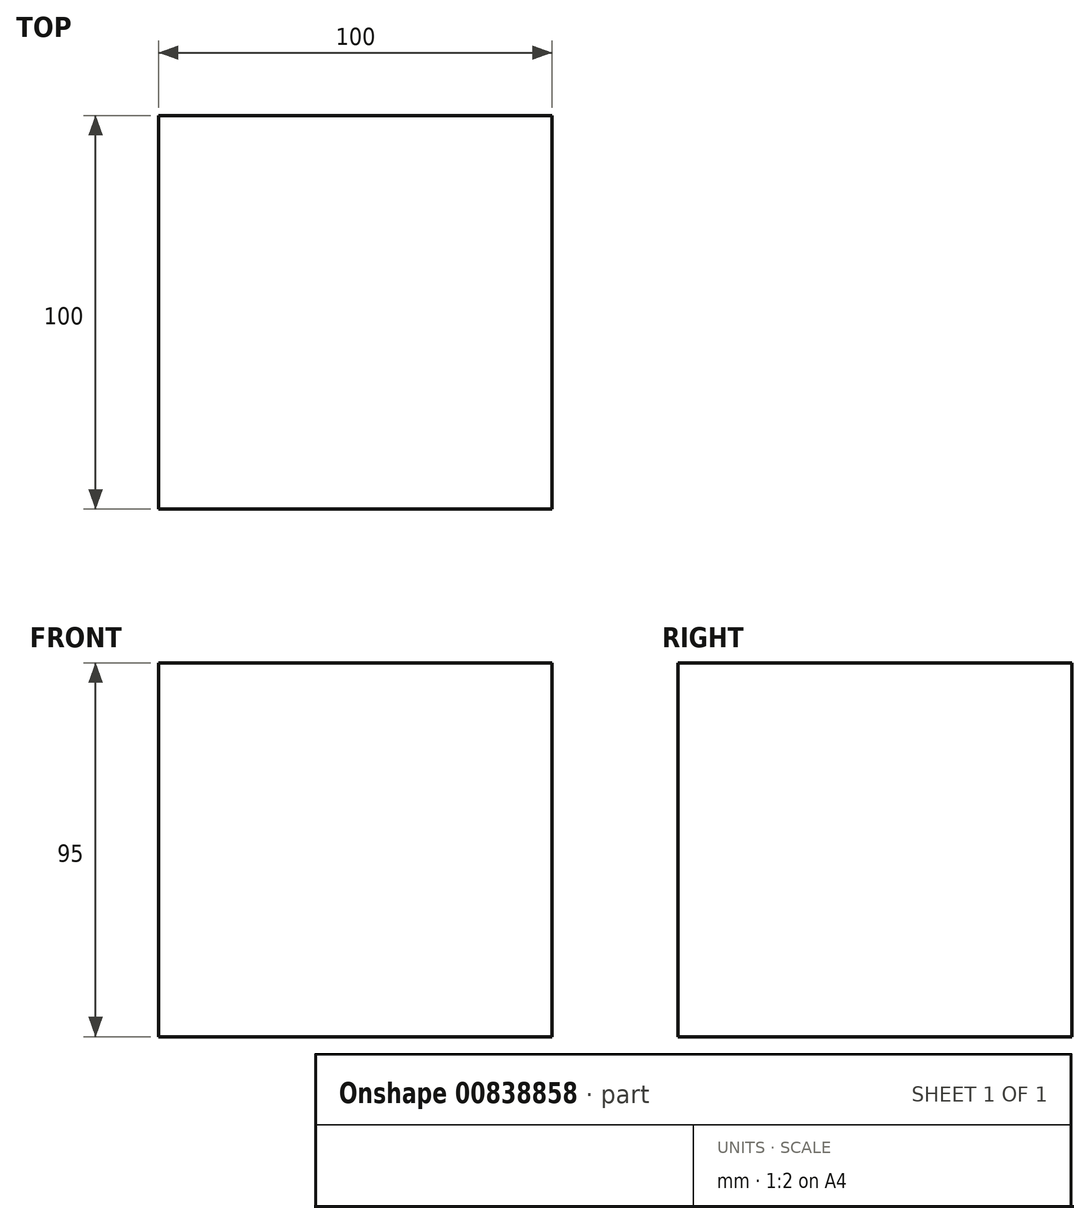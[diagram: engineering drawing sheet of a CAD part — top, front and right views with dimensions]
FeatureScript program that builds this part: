
annotation { "Feature Type Name" : "Feature", "Feature Type Description" : "" }
export const myFeature = defineFeature(function(context is Context, id is Id, definition is map)
    precondition{}
    {
        {
            var Q0;
            Q0=qCreatedBy(makeId("Top.planeOp"),FACE);
            var sketch = newSketch(context, id + "F0", { "sketchPlane" : qUnion([Q0])});
            skLineSegment(sketch, "E0.bottom", {"start": v(-50.64, 49.15) * mm, "end": v(49.36, 49.15) * mm});
            skLineSegment(sketch, "E0.top", {"start": v(-50.64, -50.85) * mm, "end": v(49.36, -50.85) * mm});
            skLineSegment(sketch, "E0.left", {"start": v(-50.64, 49.15) * mm, "end": v(-50.64, -50.85) * mm});
            skLineSegment(sketch, "E0.right", {"start": v(49.36, 49.15) * mm, "end": v(49.36, -50.85) * mm});
            skSolve(sketch);
        }
        {
            var Q0;
            Q0 = qSketchRegion(id + "F0", true);
            extrude(context, id + "F1", {"entities" : qUnion([Q0]), "depth" : 95 * mm, "offsetDistance" : 25 * mm});
        }
    });
